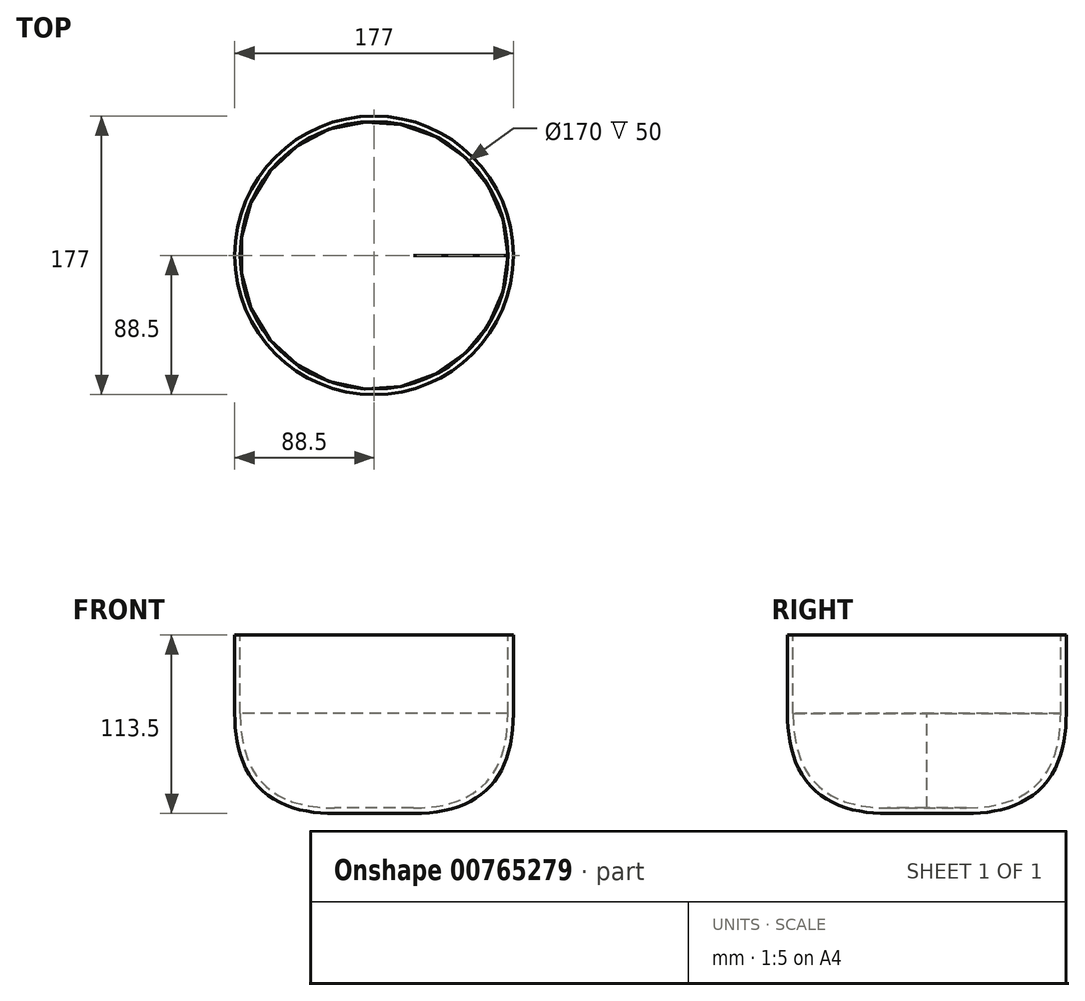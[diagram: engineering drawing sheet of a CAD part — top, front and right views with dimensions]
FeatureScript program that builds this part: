
annotation { "Feature Type Name" : "Feature", "Feature Type Description" : "" }
export const myFeature = defineFeature(function(context is Context, id is Id, definition is map)
    precondition{}
    {
        {
            var Q0;
            Q0=qCreatedBy(makeId("Front.planeOp"),FACE);
            var sketch = newSketch(context, id + "F0", { "sketchPlane" : qUnion([Q0])});
            skLineSegment(sketch, "E0", {"start": v(0, 62.28) * mm, "end": v(85, 62.28) * mm});
            skLineSegment(sketch, "E1", {"start": v(85, 62.28) * mm, "end": v(85, -47.72) * mm});
            skLineSegment(sketch, "E2", {"start": v(85, -47.72) * mm, "end": v(0, -47.72) * mm});
            skLineSegment(sketch, "E3", {"start": v(0, 62.28) * mm, "end": v(0, -47.72) * mm});
            skSolve(sketch);
        }
        {
            var Q0;
            Q0 = qSketchRegion(id + "F0", true);
            var Q1;
            Q1=sQuery(id+"F0.wireOp",EDGE,"E3");
            revolve(context, id + "F1", {"surfaceOperationType" : NewSurfaceOperationType.NEW, "entities" : qUnion([Q0]), "axis" : qUnion([Q1]), "revolveType" : RevolveType.FULL});
        }
        {
            var Q0;
            Q0=makeQuery(id+"F1.opRevolve","SWEPT_FACE",FACE,{"disambiguationData":[OSD([sQuery(id+"F0.wireOp",EDGE,"E2")])]});
            fillet(context, id + "F2", {"entities" : qUnion([Q0]), "radius" : 60 * mm, "tangentPropagation" : true, "rho" : 0.5, "crossSection" : FilletCrossSection.CONIC, "allowEdgeOverflow" : false});
        }
        {
            var Q0;
            Q0=makeQuery(id+"F1.opRevolve","SWEPT_FACE",FACE,{"disambiguationData":[OSD([sQuery(id+"F0.wireOp",EDGE,"E0")])]});
            shell(context, id + "F3", {"entities" : qUnion([Q0]), "thickness" : 3.5 * mm, "oppositeDirection" : true});
        }
        {
            var Q0;
            Q0=qCreatedBy(makeId("Front.planeOp"),FACE);
            var sketch = newSketch(context, id + "F4", { "sketchPlane" : qUnion([Q0])});
            skLineSegment(sketch, "E4", {"start": v(88.64, 62.64) * mm, "end": v(98.64, 62.64) * mm});
            skFitSpline(sketch, "E5", {"points": [v(98.64, 62.64) * mm, v(94.63, -57.4) * mm, v(100.52, -59.09) * mm], "startDerivative": vector(-27.41, -295.87) * mm, "endDerivative": vector(49.94, 31.8) * mm});
            skLineSegment(sketch, "E6", {"start": v(0, 65.82) * mm, "end": v(0, -59.18) * mm});
            skSolve(sketch);
        }
        {
            var Q0;
            Q0=sQuery(id+"F4.wireOp",EDGE,"E5");
            var Q1;
            Q1=sQuery(id+"F4.wireOp",EDGE,"E4");
            var Q2;
            Q2=sQuery(id+"F4.wireOp",EDGE,"E6");
            revolve(context, id + "F5", {"bodyType" : ToolBodyType.SURFACE, "surfaceOperationType" : NewSurfaceOperationType.NEW, "surfaceEntities" : qUnion([Q0, Q1]), "axis" : qUnion([Q2]), "revolveType" : RevolveType.FULL});
        }
        {
            var Q0;
            Q0=makeQuery(id+"F5.opRevolve","SWEPT_EDGE",EDGE,{"disambiguationData":[OSD([sQuery(id+"F4.wireOp",VERTEX,"E4.end")])]});
            fillet(context, id + "F6", {"entities" : qUnion([Q0]), "radius" : 10 * mm, "tangentPropagation" : true, "allowEdgeOverflow" : false});
        }
        {
            var Q0;
            Q0=qCreatedBy(makeId("Top.planeOp"),FACE);
            var sketch = newSketch(context, id + "F7", { "sketchPlane" : qUnion([Q0])});
            skCircle(sketch, "E7.cCircle", {"center": v(0, 0) * mm, "radius": 100.71 * mm, "construction": true});
            skLineSegment(sketch, "E7.0", {"start": v(-59.25, 81.44) * mm, "end": v(59.15, 81.51) * mm});
            skLineSegment(sketch, "E7.1", {"start": v(59.15, 81.51) * mm, "end": v(95.8, -31.06) * mm});
            skLineSegment(sketch, "E7.2", {"start": v(95.8, -31.06) * mm, "end": v(0.06, -100.71) * mm});
            skLineSegment(sketch, "E7.3", {"start": v(0.06, -100.71) * mm, "end": v(-95.76, -31.18) * mm});
            skLineSegment(sketch, "E7.4", {"start": v(-95.76, -31.18) * mm, "end": v(-59.25, 81.44) * mm});
            skSolve(sketch);
        }
        {
            var Q0;
            Q0=makeQuery(id+"F7.imprint","IMPRINT",FACE,{"disambiguationData":[TD([[makeQuery(id+"F7.imprint","IMPRINT",EDGE,{"derivedFrom":sQuery(id+"F7.wireOp",EDGE,"E7.0")}),-1.0]])]});
            cPlane(context, id + "F8", {"entities" : qUnion([Q0]), "cplaneType" : CPlaneType.OFFSET, "offset" : 60 * mm, "oppositeDirection" : true, "width" : 150 * mm, "height" : 150 * mm});
        }
    });
